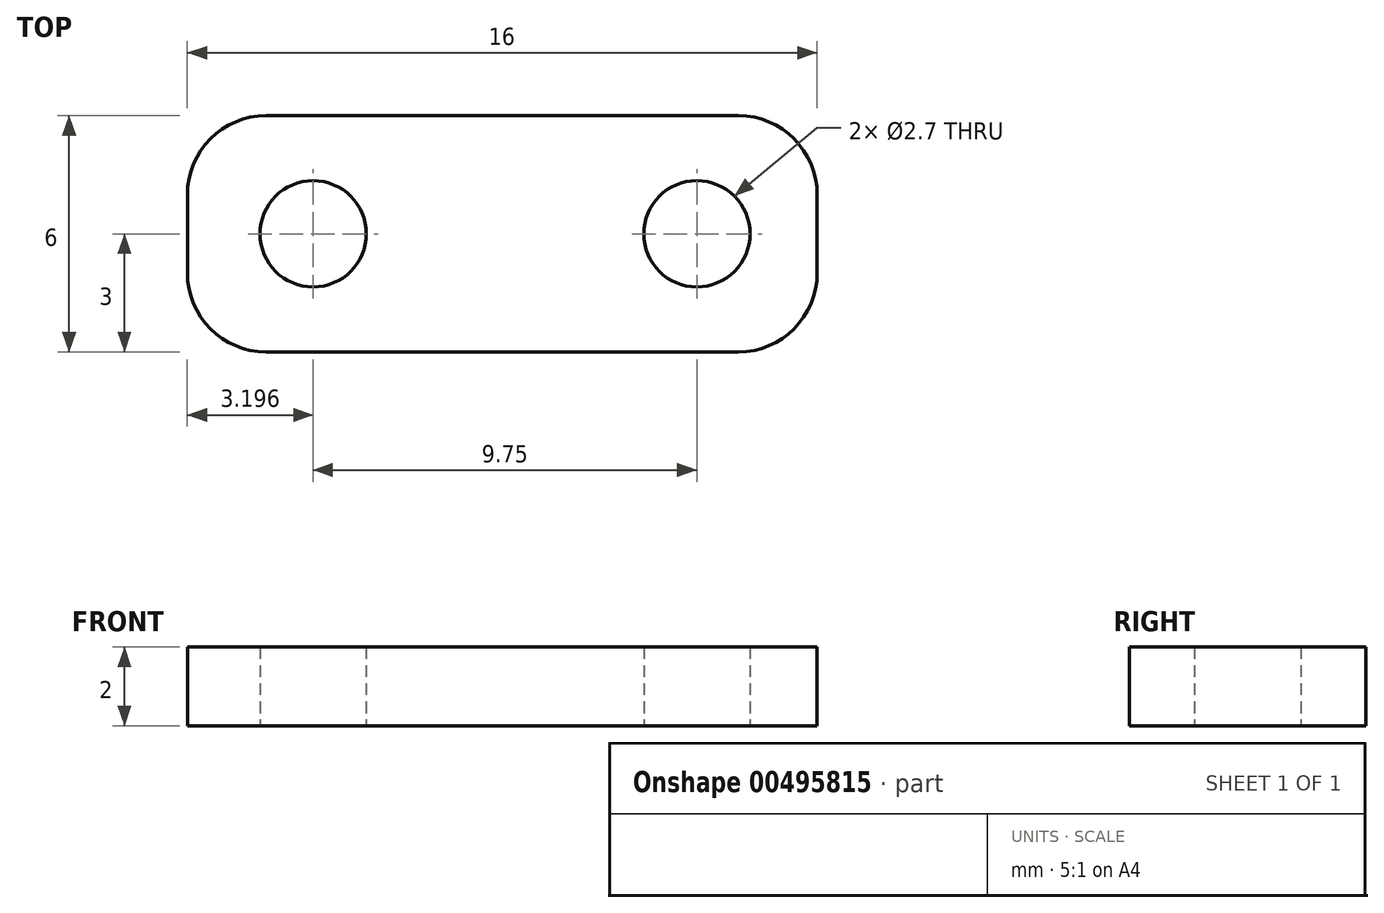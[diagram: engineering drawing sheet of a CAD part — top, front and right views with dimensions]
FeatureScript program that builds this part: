
annotation { "Feature Type Name" : "Feature", "Feature Type Description" : "" }
export const myFeature = defineFeature(function(context is Context, id is Id, definition is map)
    precondition{}
    {
        {
            var Q0;
            Q0=qCreatedBy(makeId("Top.planeOp"),FACE);
            var sketch = newSketch(context, id + "F0", { "sketchPlane" : qUnion([Q0])});
            skLineSegment(sketch, "E0.bottom", {"start": v(-59.82, 0) * mm, "end": v(-43.82, 0) * mm});
            skLineSegment(sketch, "E0.top", {"start": v(-59.82, 6) * mm, "end": v(-43.82, 6) * mm});
            skLineSegment(sketch, "E0.left", {"start": v(-59.82, 0) * mm, "end": v(-59.82, 6) * mm});
            skLineSegment(sketch, "E0.right", {"start": v(-43.82, 0) * mm, "end": v(-43.82, 6) * mm});
            skCircle(sketch, "E1", {"center": v(-56.62, 3) * mm, "radius": 1.35 * mm});
            skPoint(sketch, "E1.centerSnap0", {"position": v(-59.82, 3) * mm});
            skCircle(sketch, "E2", {"center": v(-46.87, 3) * mm, "radius": 1.35 * mm});
            skSolve(sketch);
        }
        {
            var Q0;
            Q0=makeQuery(id+"F0.imprint","IMPRINT",FACE,{"disambiguationData":[TD([[makeQuery(id+"F0.imprint","IMPRINT",EDGE,{"derivedFrom":sQuery(id+"F0.wireOp",EDGE,"E0.bottom")}),1.0]])]});
            extrude(context, id + "F1", {"entities" : qUnion([Q0]), "depth" : 2 * mm});
        }
        {
            var Q0;
            Q0=makeQuery(id+"F1.opExtrude","SWEPT_EDGE",EDGE,{"disambiguationData":[OSD([sQuery(id+"F0.wireOp",EDGE,"E0.bottom"),sQuery(id+"F0.wireOp",EDGE,"E0.left")])]});
            var Q1;
            Q1=makeQuery(id+"F1.opExtrude","SWEPT_EDGE",EDGE,{"disambiguationData":[OSD([sQuery(id+"F0.wireOp",EDGE,"E0.top"),sQuery(id+"F0.wireOp",EDGE,"E0.left")])]});
            var Q2;
            Q2=makeQuery(id+"F1.opExtrude","SWEPT_EDGE",EDGE,{"disambiguationData":[OSD([sQuery(id+"F0.wireOp",EDGE,"E0.top"),sQuery(id+"F0.wireOp",EDGE,"E0.right")])]});
            var Q3;
            Q3=makeQuery(id+"F1.opExtrude","SWEPT_EDGE",EDGE,{"disambiguationData":[OSD([sQuery(id+"F0.wireOp",EDGE,"E0.bottom"),sQuery(id+"F0.wireOp",EDGE,"E0.right")])]});
            fillet(context, id + "F2", {"entities" : qUnion([Q0, Q1, Q2, Q3]), "radius" : 2 * mm, "tangentPropagation" : true, "allowEdgeOverflow" : false});
        }
    });
